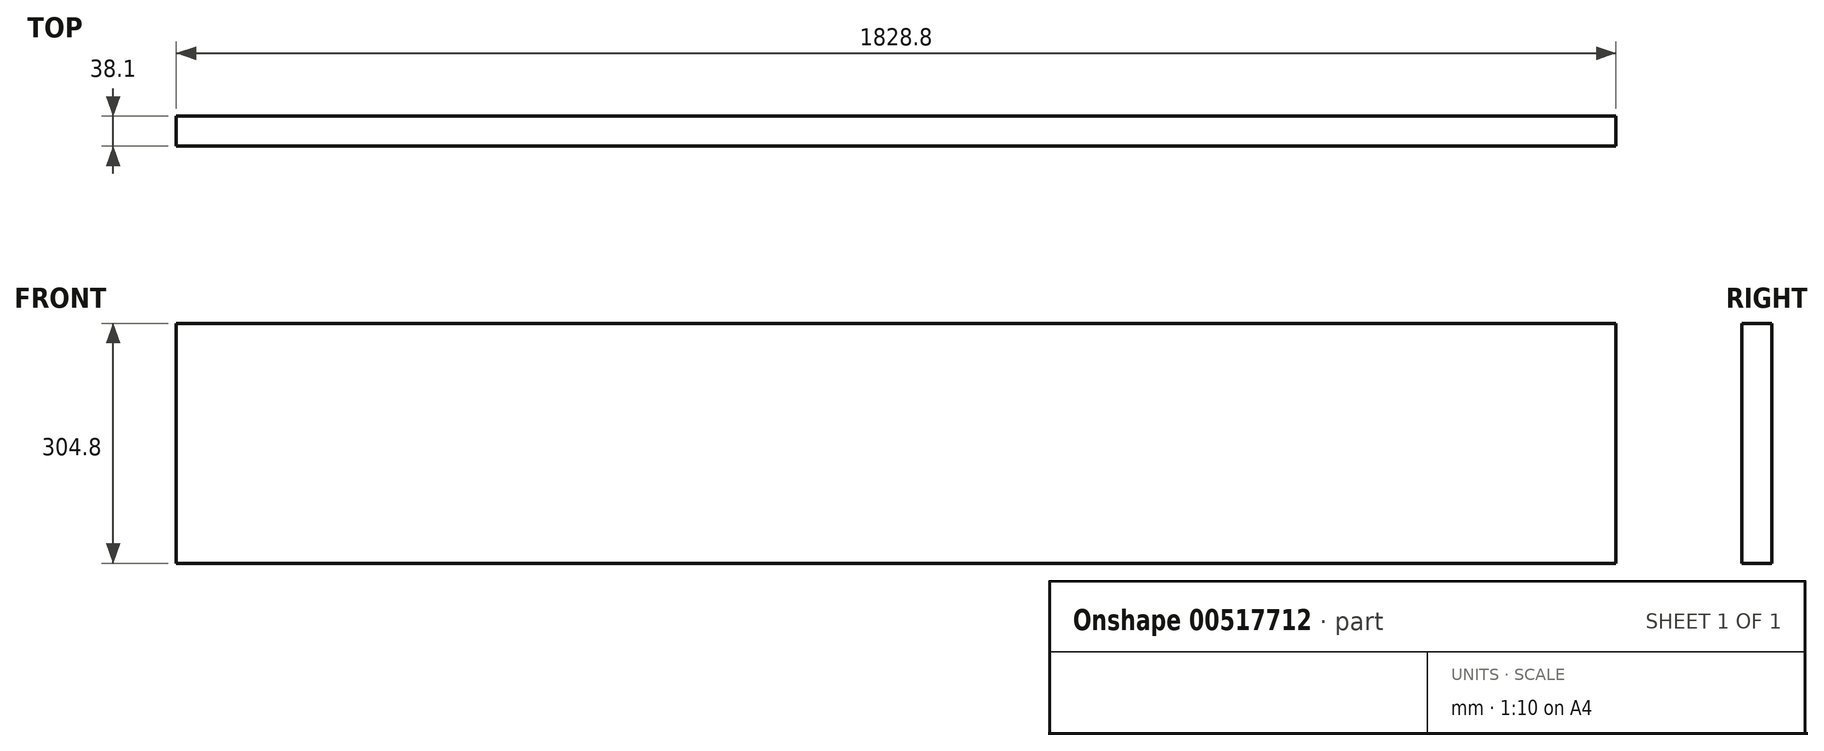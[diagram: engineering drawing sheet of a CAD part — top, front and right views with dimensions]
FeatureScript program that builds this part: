
annotation { "Feature Type Name" : "Feature", "Feature Type Description" : "" }
export const myFeature = defineFeature(function(context is Context, id is Id, definition is map)
    precondition{}
    {
        {
            var Q0;
            Q0=qCreatedBy(makeId("Front.planeOp"),FACE);
            var sketch = newSketch(context, id + "F0", { "sketchPlane" : qUnion([Q0])});
            skLineSegment(sketch, "E0.bottom", {"start": v(914.4, 152.4) * mm, "end": v(-914.4, 152.4) * mm});
            skLineSegment(sketch, "E0.top", {"start": v(914.4, -152.4) * mm, "end": v(-914.4, -152.4) * mm});
            skLineSegment(sketch, "E0.left", {"start": v(914.4, 152.4) * mm, "end": v(914.4, -152.4) * mm});
            skLineSegment(sketch, "E0.right", {"start": v(-914.4, 152.4) * mm, "end": v(-914.4, -152.4) * mm});
            skPoint(sketch, "E0.middle", {"position": v(0, 0) * mm});
            skSolve(sketch);
        }
        {
            var Q0;
            Q0 = qSketchRegion(id + "F0", true);
            extrude(context, id + "F1", {"entities" : qUnion([Q0]), "depth" : 38.1 * mm, "offsetDistance" : 25.4 * mm});
        }
    });
